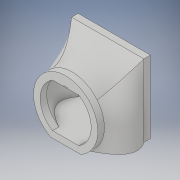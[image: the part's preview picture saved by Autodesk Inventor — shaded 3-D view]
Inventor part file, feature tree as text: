
AUTODESK INVENTOR PART (.ipt)
format: ipt  version: 2017 (Build 210142000, 142)  size: 411,136 bytes
history: native  units: in
note: dims shown in document units (in); Inventor stores cm internally (conversion verified against a paired STEP export)
features: sketch x4, extrude x3, other x2, loft x2
ambient origin geometry x8: Origin, YZ Plane, XZ Plane, XY Plane, X Axis, Y Axis, Z Axis, Center Point
bodies: Solid1 (feature_tree), Solid3 (feature_tree)
feature tree (11):
  extrude  "connection"  Depth=1.0in
  other  "front half of room"
  other  "front of room"
  sketch  "Sketch3"  dims[d17=2.7in d26=69.0in d27=59.0in d33=1.0in d34=1.0in]
  loft  "shell make "
  loft  "shell cut"
  extrude  "connection to door"  Depth=1.0in
  extrude  "light"  Depth=1.0in
  sketch  "Sketch1"  dims[d12=1.0in d13=0.0in d14=2.7in]
  sketch  "Sketch5"  dims[d35=1.0in d36=1.0in]
  sketch  "Sketch12"  dims[d82=4.0in d83=1.0in d84=4.8944in d85=0.5833in d86=3.8873in d87=3.8873in d88=1.7083in d89=0.0625in d90=0.0625in d91=1.6458in d92=0.125in d93=0.125in d153=6.21in d154=5.31in d157=0.0in d158=90.0deg d159=0.0in d160=90.0deg d161=0.0in d162=90.0deg d180=0.0in d181=90.0deg d182=0.0in d183=90.0deg d184=0.0in d185=90.0deg d217=3.082in d219=1.0in d220=1.0in d221=9.0in d222=9.0in d223=1.0in d233=0.25in d234=0.125in d235=45.0deg d236=0.0892in d237=0.0884in d238=0.0482in d239=1.0in d240=0.0in d241=1.0in d242=1.0in d243=1.0in d244=1.0in d245=1.0in d246=0.0in]
